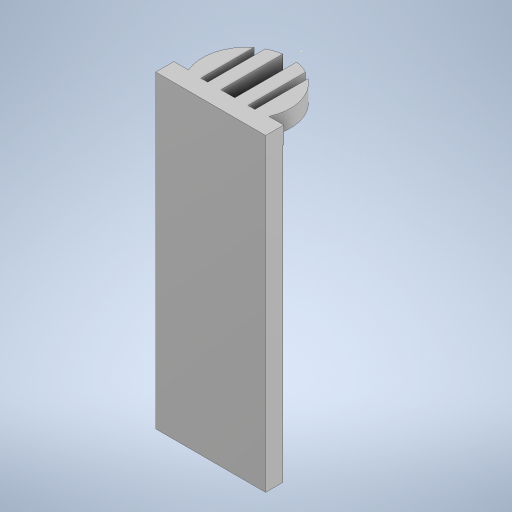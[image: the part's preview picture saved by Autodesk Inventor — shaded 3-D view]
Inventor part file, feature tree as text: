
AUTODESK INVENTOR PART (.ipt)
format: ipt  version: 2023 (Build 270158030, 158C)  size: 1,324,032 bytes
history: mixed  units: in
note: dims shown in document units (in); Inventor stores cm internally (conversion verified against a paired STEP export)
features: other x43, move_body x11, direct_edit x6, sketch x5, extrude x4, projected_geometry x2, imported_body x1
ambient origin geometry x8: Origin, YZ Plane, XZ Plane, XY Plane, X Axis, Y Axis, Z Axis, Center Point
bodies: Solid1 (imported_parasolid), Solid2 (imported_parasolid), Solid3 (imported_parasolid), Solid4 (imported_parasolid), Solid5 (imported_parasolid), Solid6 (imported_parasolid), Solid7 (imported_parasolid), Solid8 (imported_parasolid), Solid9 (imported_parasolid), Solid10 (imported_parasolid), Solid11 (imported_parasolid), Solid12 (imported_parasolid), Solid13 (imported_parasolid), Solid14 (imported_parasolid), Solid15 (imported_parasolid), Solid16 (imported_parasolid), Solid17 (imported_parasolid), Solid18 (imported_parasolid), Solid19 (imported_parasolid), Solid20 (imported_parasolid), Solid21 (imported_parasolid), Solid22 (imported_parasolid), Solid23 (imported_parasolid), Solid24 (imported_parasolid), Solid25 (imported_parasolid), Solid26 (imported_parasolid), Solid27 (imported_parasolid), Solid28 (imported_parasolid), Solid29 (imported_parasolid), Solid30 (imported_parasolid), Solid31 (imported_parasolid), Solid32 (imported_parasolid), Solid33 (imported_parasolid), Solid34 (imported_parasolid), Solid35 (imported_parasolid), Solid36 (imported_parasolid), Solid37 (imported_parasolid), Solid38 (imported_parasolid), Solid39 (imported_parasolid), Solid40 (imported_parasolid), Solid41 (imported_parasolid), Solid42 (imported_parasolid), Solid43 (imported_parasolid)
feature tree (72):
  direct_edit  "Direct Edit1"
  direct_edit  "Direct Edit2"
  direct_edit  "Direct Edit3"
  direct_edit  "Direct Edit4"
  direct_edit  "Direct Edit5"
  direct_edit  "Direct Edit6"
  extrude  "Extrusion1"  Depth=1.2205in TaperAngle=0.0deg
  extrude  "Extrusion2"  TaperAngle=0.0deg  [1 undecoded]
  extrude  "Extrusion3"  TaperAngle=0.0deg  [1 undecoded]
  sketch  "Sketch4"  dims[d18=0.0in d19=0.0in d20=0.1181in d21=0.0in d22=0.0in d23=0.0394in]
  extrude  "Extrusion5"  Depth=0.0394in TaperAngle=0.0deg
  sketch  "Sketch1"  dims[d0=0.0in d1=0.0in d2=1.2205in d3=0.0in d4=0.0in d5=1.2205in]
  sketch  "Sketch2"  dims[d6=0.0in d7=0.0in d8=3.4055in d9=0.0in d10=0.0in d11=-0.0945in]
  projected_geometry  "Projected Loop1"
  sketch  "Sketch3"  dims[d12=0.0in d13=0.0in d14=-0.0394in d15=0.0in d16=0.0in d17=-0.0394in]
  projected_geometry  "Projected Loop2"
  sketch  "Sketch5"  dims[d24=0.0in d25=0.0in d26=0.0394in d27=0.0394in d28=0.0394in d29=0.0394in d30=0.0394in d31=0.0in d32=0.0in d33=0.1681in d34=0.0in d35=0.1681in d36=0.0in d40=0.0in d41=0.0in d42=-0.1969in d43=0.0in d44=0.0in d45=-0.1969in d46=3.5433in d47=0.3937in d48=0.0in d49=1.9685in]
  other  "Rat_ToothHolder"
  other  "StandExtention"
  other  "CableHolderPlate"
  other  "Mouse_ToothHolder"
  other  "Base_Joint1"
  other  "MouseEarbar"
  other  "MouseEarbar (1)"
  other  "PreampPlate"
  other  "CableHolderTop"
  other  "MouseNoseCone"
  other  "HeadFixClamp"
  other  "HEadFixBase"
  other  "HeadFixBase2"
  other  "HeadFixClamp2"
  other  "Base_Joint2"
  other  "CableHolderArm1"
  other  "CableHolderArm2"
  other  "CableHolderClamp2"
  other  "CableHolderArm4"
  other  "CableHolderArm3"
  other  "NoseConeStand (1) (2)"
  other  "PET-attach"
  other  "RatNoseCone"
  other  "Holder_For_Odor_Delivery"
  other  "MouseHeadCapBase"
  other  "MouseHeadCapBase_I"
  other  "MouseHeadCapBase_II"
  other  "MouseHeadCapBase_III"
  other  "BedTop (1)"
  other  "BedSpacer (1) (1)"
  other  "BedSpacer (2) (1)"
  other  "BedSpacer (3) (1)"
  other  "BedSpacer (4)"
  other  "BedBottom (1)"
  other  "Mouse restrainer"
  other  "Resterainer pusher"
  other  "RatEarbar_1"
  other  "RatEarbar_2"
  other  "Base_Joint1 (1) (1)"
  other  "Base_Joint1 (1) (1) (1)"
  other  "Base_Joint1 (1)"
  other  "Base (1) (1)"
  other  "Base_Joint2 (1)"
  move_body  "Move1"
  move_body  "Move2"
  move_body  "Move3"
  move_body  "Move4"
  move_body  "Move5"
  move_body  "Move6"
  move_body  "Move7"
  move_body  "Move8"
  move_body  "Move9"
  move_body  "Move10"
  move_body  "Move11"
  imported_body  NMx_Import_Brep_tag  [imported B-rep: ~24 faces, bbox_mm=[31.999988, 90.0, 23.042784]]
note: 2 required parameter values undecoded (feature->parameter linkage not recoverable at this tier; creation-order binding heuristic only, values carry confidence <= 0.55)
